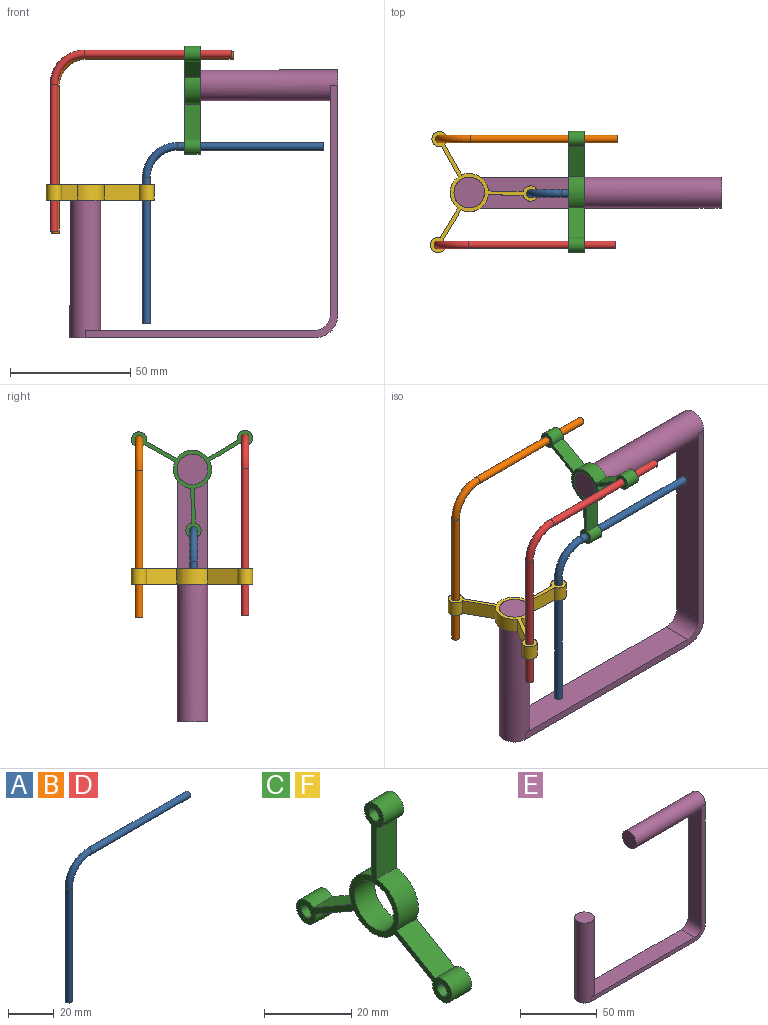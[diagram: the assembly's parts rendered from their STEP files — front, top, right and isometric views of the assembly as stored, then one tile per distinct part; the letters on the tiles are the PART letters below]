
ASSEMBLY  parts=6 mates=8
PART A: 5 faces, bbox 76.4x3.2x76.4 mm
  f0: plane 3.18x3.18mm, normal (1,0,0), area 7.9mm2, adj f2
  f1: plane 3.18x3.18mm, normal (0,0,-1), area 7.9mm2, adj f4
  f2: cylinder r=1.59mm len=60.96mm, axis (-1,0,0), area 608mm2, adj f0,f3
  f3: torus R=12.7mm, axis (0,-1,0), area 199mm2, adj f2,f4
  f4: cylinder r=1.59mm len=60.96mm, axis (0,0,-1), area 608mm2, adj f1,f3
PART B: same geometry as A
PART C: 18 faces, bbox 6.4x50.3x44.5 mm
  f0: cylinder r=7.94mm len=11.16mm, axis (-1,0,0), area 95.5mm2, adj f4,f5,f7,f14
  f1: cylinder r=7.94mm len=12.89mm, axis (-1,0,0), area 95.5mm2, adj f4,f5,f10,f15
  f2: cylinder r=6.35mm len=12.7mm, axis (-1,0,0), area 253.4mm2, adj f4,f5
  f3: cylinder r=7.94mm len=11.16mm, axis (-1,0,0), area 95.5mm2, adj f4,f5,f6,f11
  f4: plane 50.34x44.45mm, normal (1,0,0), area 210.8mm2, adj f0,f1,f2,f3,f6,f7,f8,f9
  f5: plane 50.34x44.45mm, normal (-1,0,0), area 210.8mm2, adj f0,f1,f2,f3,f6,f7,f8,f9
  f6: plane 14.43x6.35mm, normal (0,-1,0), area 91.6mm2, adj f3,f4,f5,f8
  f7: plane 14.43x6.35mm, normal (0,1,0), area 91.6mm2, adj f0,f4,f5,f8
  f8: cylinder r=3.17mm len=6.35mm, axis (-1,0,0), area 116.5mm2, adj f4,f5,f6,f7
  f9: cylinder r=1.59mm len=6.35mm, axis (-1,0,0), area 63.3mm2, adj f4,f5
  f10: plane 12.5x7.21mm, normal (0,0.5,-0.87), area 91.6mm2, adj f1,f4,f5,f12
  f11: plane 12.5x7.21mm, normal (0,-0.5,0.87), area 91.6mm2, adj f3,f4,f5,f12
  f12: cylinder r=3.17mm len=6.35mm, axis (-1,0,0), area 116.5mm2, adj f4,f5,f10,f11
  f13: cylinder r=1.59mm len=6.35mm, axis (-1,0,0), area 63.3mm2, adj f4,f5
  f14: plane 12.5x7.21mm, normal (0,0.5,0.87), area 91.6mm2, adj f0,f4,f5,f16
  f15: plane 12.5x7.21mm, normal (0,-0.5,-0.87), area 91.6mm2, adj f1,f4,f5,f16
  f16: cylinder r=3.17mm len=6.35mm, axis (-1,0,0), area 116.5mm2, adj f4,f5,f14,f15
  f17: cylinder r=1.59mm len=6.35mm, axis (-1,0,0), area 63.3mm2, adj f4,f5
PART D: same geometry as A
PART E: 12 faces, bbox 111.1x12.7x111.1 mm
  f0: plane 101.6x12.7mm, normal (0,0,-1), area 1273mm2, adj f4,f5,f8,f11
  f1: plane 101.6x12.7mm, normal (1,0,0), area 1273mm2, adj f4,f5,f6,f11
  f2: plane 95.25x12.7mm, normal (-1,0,0), area 1146.3mm2, adj f4,f5,f6,f10
  f3: plane 95.25x12.7mm, normal (0,0,1), area 1146.3mm2, adj f4,f5,f8,f10
  f4: plane 104.78x104.78mm, normal (0,-1,0), area 644.4mm2, adj f0,f1,f2,f3,f6,f8,f10,f11
  f5: plane 104.78x104.78mm, normal (0,1,0), area 644.4mm2, adj f0,f1,f2,f3,f6,f8,f10,f11
  f6: cylinder r=6.35mm len=63.5mm, axis (1,0,0), area 2470.2mm2, adj f1,f2,f4,f5,f7
  f7: plane 12.7x12.7mm, normal (-1,0,0), area 126.7mm2, adj f6
  f8: cylinder r=6.35mm len=63.5mm, axis (0,0,-1), area 2470.2mm2, adj f0,f3,f4,f5,f9
  f9: plane 12.7x12.7mm, normal (0,0,1), area 126.7mm2, adj f8
  f10: cylinder r=6.35mm len=12.7mm, axis (0,1,0), area 126.7mm2, adj f2,f3,f4,f5
  f11: cylinder r=9.53mm len=12.7mm, axis (0,1,0), area 190mm2, adj f0,f1,f4,f5
PART F: same geometry as C
PLACE A t=(48.26,-0.39,-50.8)mm
PLACE B t=(10.5,22.19,-13.04)mm
PLACE C rot(axis=(1,0,0),59.1deg) t=(0,87.19,49.44)mm
PLACE D t=(9.82,-21.8,-12.36)mm
PLACE E at identity fixed
PLACE F rot(axis=(0.01,1,-0.01),90deg) t=(-203.19,1.58,0)mm
MATE cylindrical F.f13 <-> D.f4  axis (0,0,1) through (-114.64,-21.8,60.32)mm
MATE cylindrical F.f9 <-> A.f4  axis (0,0,1) through (-76.2,-0.39,60.32)mm
MATE cylindrical F.f17 <-> B.f4  axis (0,0,1) through (-113.96,22.19,60.32)mm
MATE cylindrical C.f17 <-> B.f2  axis (-1,0,0) through (-60.32,22.19,113.96)mm
MATE cylindrical C.f9 <-> D.f2  axis (1,0,0) through (-53.97,-21.8,114.64)mm
MATE revolute C.f0 <-> E.f6  axis (-1,0,0) through (-60.32,0,101.6)mm
MATE cylindrical C.f13 <-> A.f2  axis (-1,0,0) through (-60.32,-0.39,76.2)mm
MATE revolute F.f0 <-> E.f8  axis (0,0,1) through (-101.6,0,60.32)mm
